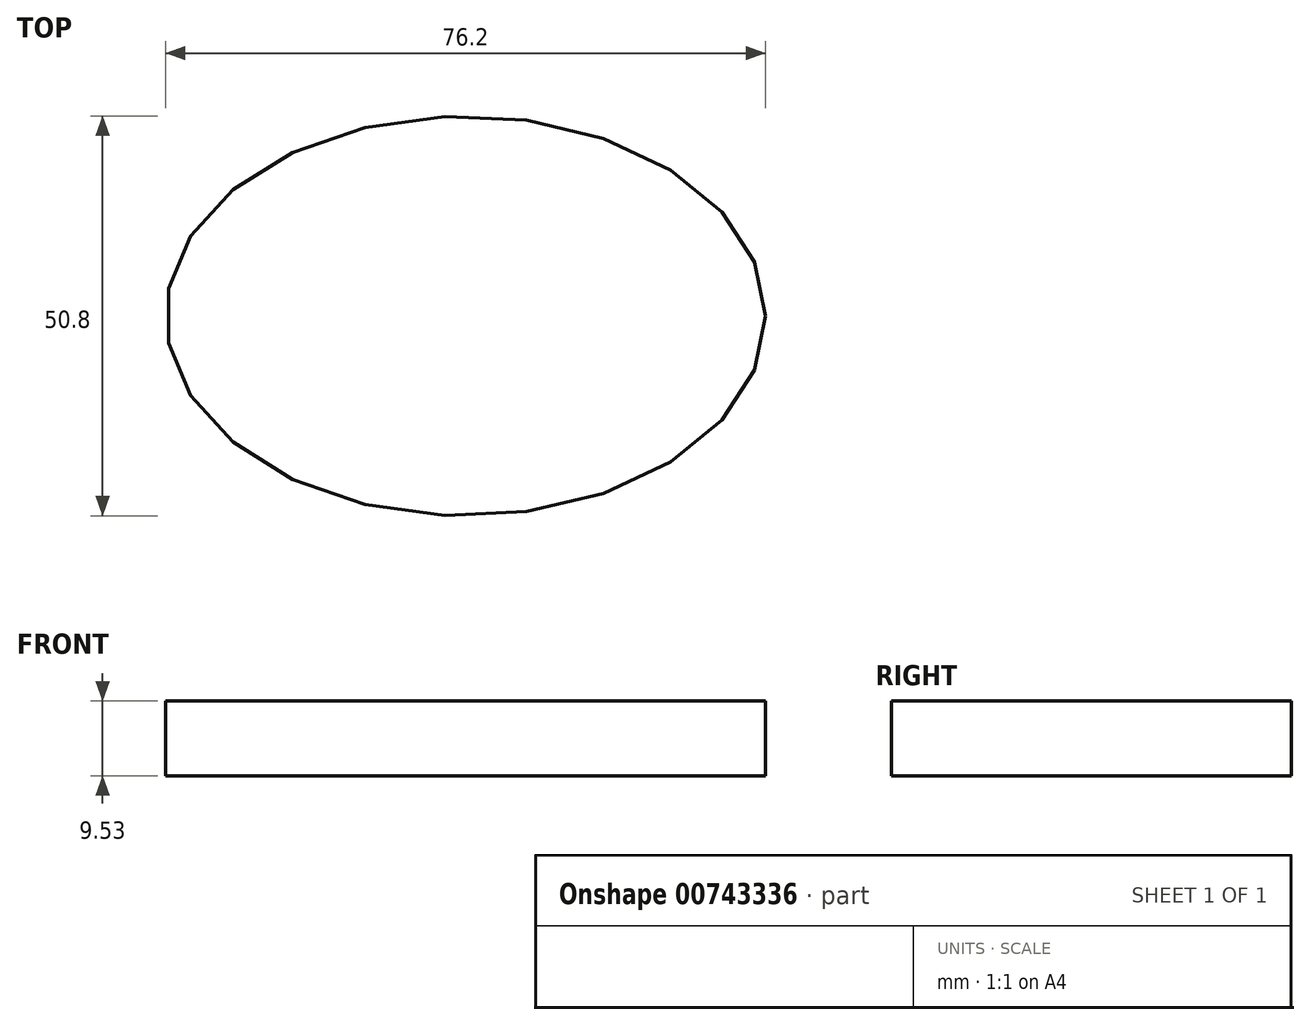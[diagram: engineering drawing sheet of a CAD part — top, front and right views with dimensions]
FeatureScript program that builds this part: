
annotation { "Feature Type Name" : "Feature", "Feature Type Description" : "" }
export const myFeature = defineFeature(function(context is Context, id is Id, definition is map)
    precondition{}
    {
        {
            var Q0;
            Q0=qCreatedBy(makeId("Top.planeOp"),FACE);
            var sketch = newSketch(context, id + "F0", { "sketchPlane" : qUnion([Q0])});
            skEllipse(sketch, "E0", {"center": v(0, 0) * mm, "majorRadius": 38.1 * mm, "minorRadius": 25.4 * mm, "majorAxis": v(1, 0)});
            skSolve(sketch);
        }
        {
            var Q0;
            Q0 = qSketchRegion(id + "F0", true);
            extrude(context, id + "F1", {"entities" : qUnion([Q0]), "depth" : 9.52 * mm, "offsetDistance" : 25.4 * mm});
        }
    });
